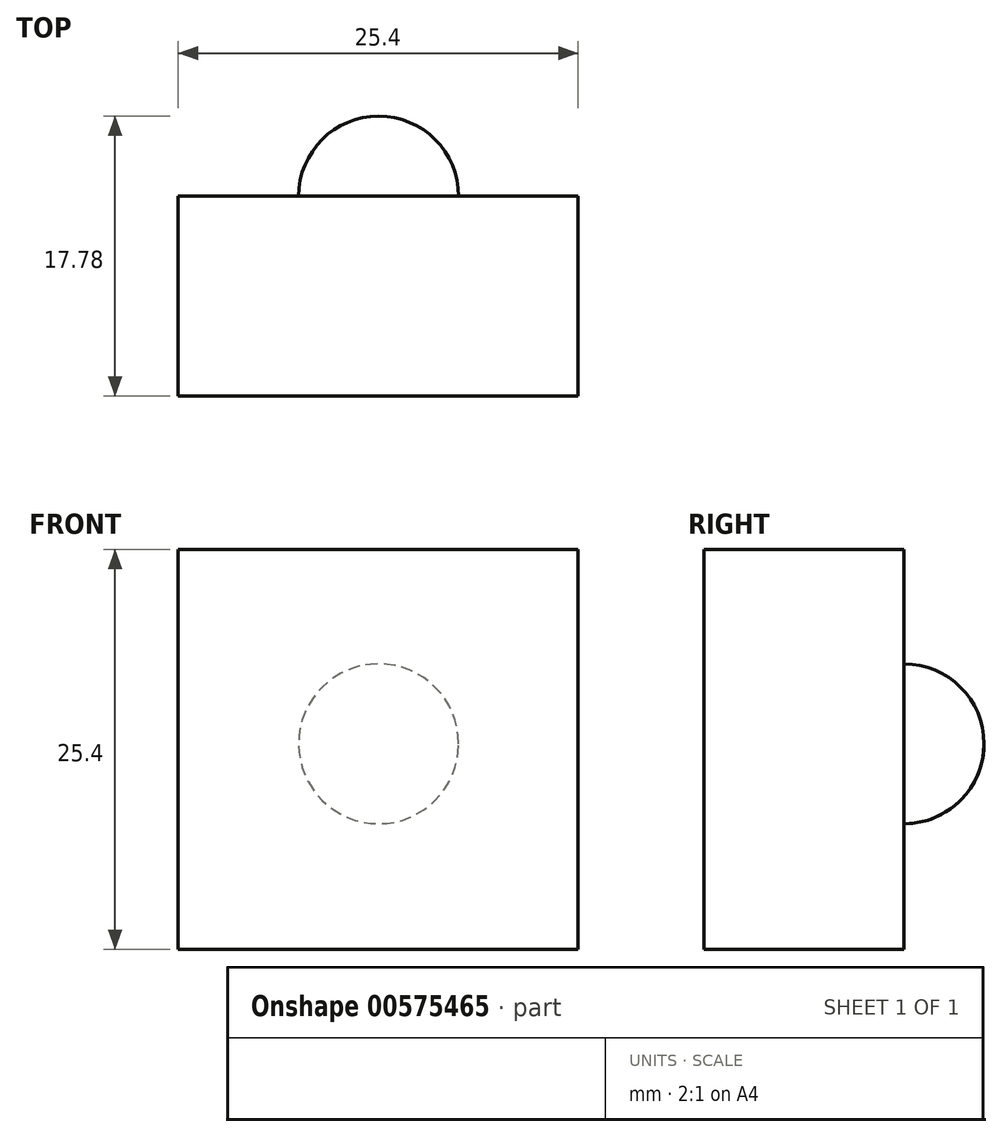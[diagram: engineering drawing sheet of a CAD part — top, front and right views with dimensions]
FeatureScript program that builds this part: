
annotation { "Feature Type Name" : "Feature", "Feature Type Description" : "" }
export const myFeature = defineFeature(function(context is Context, id is Id, definition is map)
    precondition{}
    {
        {
            var Q0;
            Q0=qCreatedBy(makeId("Front.planeOp"),FACE);
            var sketch = newSketch(context, id + "F0", { "sketchPlane" : qUnion([Q0])});
            skLineSegment(sketch, "E0.bottom", {"start": v(11.73, 12.34) * mm, "end": v(37.13, 12.34) * mm});
            skLineSegment(sketch, "E0.top", {"start": v(11.73, -13.06) * mm, "end": v(37.13, -13.06) * mm});
            skLineSegment(sketch, "E0.left", {"start": v(11.73, 12.34) * mm, "end": v(11.73, -13.06) * mm});
            skLineSegment(sketch, "E0.right", {"start": v(37.13, 12.34) * mm, "end": v(37.13, -13.06) * mm});
            skSolve(sketch);
        }
        {
            var Q0;
            Q0 = qSketchRegion(id + "F0", true);
            extrude(context, id + "F1", {"entities" : qUnion([Q0]), "depth" : 12.7 * mm, "offsetDistance" : 25.4 * mm});
        }
        {
            var Q0;
            Q0=qCreatedBy(makeId("Front.planeOp"),FACE);
            var sketch = newSketch(context, id + "F2", { "sketchPlane" : qUnion([Q0])});
            skCircle(sketch, "E1", {"center": v(24.46, 0) * mm, "radius": 5.08 * mm});
            skSolve(sketch);
        }
        {
            var Q0;
            Q0 = qSketchRegion(id + "F2", true);
            extrude(context, id + "F3", {"entities" : qUnion([Q0]), "operationType" : NewBodyOperationType.ADD, "oppositeDirection" : true, "depth" : 5.08 * mm, "offsetDistance" : 25.4 * mm});
        }
        {
            var Q0;
            Q0=makeQuery(id+"F3.opExtrude","CAP_EDGE",EDGE,{"disambiguationData":[OSD([sQuery(id+"F2.wireOp",EDGE,"E1")])],"isStart":false});
            fillet(context, id + "F4", {"entities" : qUnion([Q0]), "radius" : 5.08 * mm, "tangentPropagation" : true, "allowEdgeOverflow" : false});
        }
    });
